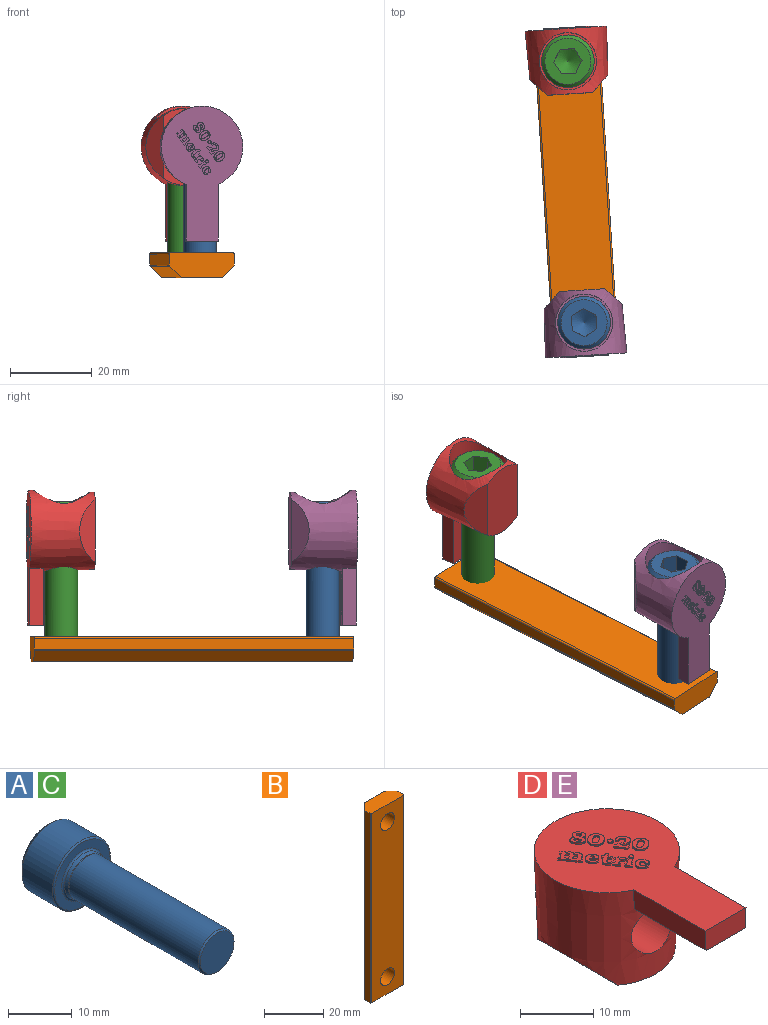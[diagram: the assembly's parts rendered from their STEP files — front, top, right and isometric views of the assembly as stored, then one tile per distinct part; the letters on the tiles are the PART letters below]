
ASSEMBLY  parts=5 mates=5
PART A: 18 faces, bbox 15x38.9x15 mm
  f0: cone r=3.48mm half-angle=60deg, axis (0,1,0), area 43.5mm2, adj f1,f2,f3,f4,f5,f6
  f1: plane 5.51x4.07mm, normal (0.5,0,0.87), area 15mm2, adj f0,f2,f6,f7
  f2: plane 5.51x4.54mm, normal (1,0,0), area 15mm2, adj f0,f1,f3,f7
  f3: plane 5.51x4.07mm, normal (0.5,0,-0.87), area 15mm2, adj f0,f2,f4,f7
  f4: plane 5.51x4.07mm, normal (-0.5,0,-0.87), area 15mm2, adj f0,f3,f5,f7
  f5: plane 5.51x4.54mm, normal (-1,0,0), area 15mm2, adj f0,f4,f6,f7
  f6: plane 5.51x4.07mm, normal (-0.5,0,0.87), area 15mm2, adj f0,f1,f5,f7
  f7: plane 11.27x11.27mm, normal (0,1,0), area 68.5mm2, adj f1,f2,f3,f4,f5,f6,f8
  f8: cone r=6.43mm half-angle=45deg, axis (0,-1,0), area 42.9mm2, adj f7,f9
  f9: cylinder r=6.43mm len=12.87mm, axis (0,-1,0), area 272.9mm2, adj f8,f10
  f10: torus R=6.17mm, axis (0,-1,0), area 16.7mm2, adj f9,f11
  f11: plane 12.33x12.33mm, normal (0,-1,0), area 52.9mm2, adj f10,f12
  f12: torus R=4.6mm, axis (0,-1,0), area 13.9mm2, adj f11,f13
  f13: cone r=4.22mm half-angle=17.9deg, axis (0,1,0), area 16.9mm2, adj f12,f15
  f14: plane 7.5x7.5mm, normal (0,-1,0), area 44.2mm2, adj f16
  f15: torus R=4.4mm, axis (0,-1,0), area 3.1mm2, adj f13,f17
  f16: cone r=4mm half-angle=45deg, axis (0,1,0), area 8.6mm2, adj f14,f17
  f17: cylinder r=4mm len=28.73mm, axis (0,-1,0), area 722.1mm2, adj f15,f16
PART B: 18 faces, bbox 15.9x6.2x78.2 mm
  f0: cylinder r=1.59mm len=3.18mm, axis (0,1,0), area 0mm2, adj f1,f10
  f1: cone r=1.59mm half-angle=59deg, axis (0,1,0), area 9.2mm2, adj f0
  f2: cylinder r=0.38mm len=78.16mm, axis (0,0,1), area 23.4mm2, adj f6,f7,f12,f14
  f3: cylinder r=0.38mm len=78.16mm, axis (0,0,1), area 23.4mm2, adj f8,f9,f12,f14
  f4: cylinder r=0.38mm len=78.16mm, axis (0,0,1), area 23.4mm2, adj f8,f10,f12,f14
  f5: cylinder r=0.38mm len=78.16mm, axis (0,0,1), area 23.4mm2, adj f7,f10,f12,f14
  f6: plane 78.16x2.64mm, normal (1,0,0), area 206.5mm2, adj f2,f11,f12,f14
  f7: plane 78.16x2.76mm, normal (0.71,0.71,0), area 304.6mm2, adj f2,f5,f12,f14
  f8: plane 78.16x2.76mm, normal (-0.71,0.71,0), area 304.6mm2, adj f3,f4,f12,f14
  f9: plane 78.16x2.64mm, normal (-1,0,0), area 206.5mm2, adj f3,f12,f13,f14
  f10: plane 78.16x9.6mm, normal (0,1,0), area 673.1mm2, adj f0,f4,f5,f12,f14,f15,f16
  f11: cylinder r=0.38mm len=78.16mm, axis (0,0,1), area 46.8mm2, adj f6,f12,f14,f17
  f12: plane 15.88x6.16mm, normal (0,0,1), area 88.8mm2, adj f2,f3,f4,f5,f6,f7,f8,f9
  f13: cylinder r=0.38mm len=78.16mm, axis (0,0,1), area 46.8mm2, adj f9,f12,f14,f17
  f14: plane 15.88x6.16mm, normal (0,0,-1), area 88.8mm2, adj f2,f3,f4,f5,f6,f7,f8,f9
  f15: cylinder r=3.32mm len=6.65mm, axis (0,-1,0), area 128.6mm2, adj f10,f17
  f16: cylinder r=3.32mm len=6.65mm, axis (0,1,0), area 128.6mm2, adj f10,f17
  f17: plane 78.16x15.11mm, normal (0,-1,0), area 1111.8mm2, adj f11,f12,f13,f14,f15,f16
PART C: same geometry as A
PART D: 311 faces, bbox 20.2x33.2x16.5 mm
  f0: plane 1.75x1.49mm, normal (0,0,1), area 1.4mm2, adj f8,f9,f10,f11,f12
  f1: plane 0.82x0.69mm, normal (0,0,1), area 0.3mm2, adj f13,f14,f15,f16,f17,f18,f19,f20
  f2: plane 1.07x0.89mm, normal (0,0,1), area 0.5mm2, adj f21,f22,f23,f24,f25,f26
  f3: plane 1.75x1.49mm, normal (0,0,1), area 1.4mm2, adj f27,f28,f29,f30,f31
  f4: plane 0.6x0.53mm, normal (0,0,1), area 0.1mm2, adj f32,f33,f34
  f5: plane 0.91x0.63mm, normal (0,0,-1), area 0.3mm2, adj f35,f36,f37
  f6: plane 1.78x0.94mm, normal (0,0,-1), area 1.1mm2, adj f38,f39,f40,f41,f42
  f7: plane 0.98x0.85mm, normal (0,0,-1), area 0.6mm2, adj f43,f44,f45,f46
  f8: extruded ~1.02x0.29mm, area 0.3mm2, adj f0,f9,f12,f49
  f9: extruded ~0.91x0.54mm, area 0.3mm2, adj f0,f8,f10,f49
  f10: extruded ~1.02x0.3mm, area 0.3mm2, adj f0,f9,f11,f49
  f11: extruded ~0.39x0.25mm, area 0.1mm2, adj f0,f10,f12,f49
  f12: extruded ~0.53x0.51mm, area 0.2mm2, adj f0,f8,f11,f49
  f13: plane 0.25x0.21mm, normal (0.97,0.23,0), area 0.1mm2, adj f1,f14,f20,f50
  f14: extruded ~0.33x0.25mm, area 0.1mm2, adj f1,f13,f15,f50
  f15: cylinder r=0.19mm len=0.25mm, axis (0,0,1), area 0mm2, adj f1,f14,f16,f50
  f16: extruded ~0.4x0.25mm, area 0.1mm2, adj f1,f15,f17,f50
  f17: extruded ~0.46x0.25mm, area 0.1mm2, adj f1,f16,f18,f50
  f18: extruded ~0.25x0.19mm, area 0.1mm2, adj f1,f17,f19,f50
  f19: extruded ~0.25x0.14mm, area 0mm2, adj f1,f18,f20,f50
  f20: plane 0.25x0.1mm, normal (0.13,0.99,0), area 0mm2, adj f1,f13,f19,f50
  f21: plane 0.28x0.25mm, normal (-0.97,-0.23,0), area 0.1mm2, adj f2,f22,f26,f50
  f22: extruded ~0.35x0.25mm, area 0.1mm2, adj f2,f21,f23,f50
  f23: extruded ~0.25x0.14mm, area 0mm2, adj f2,f22,f24,f50
  f24: extruded ~0.51x0.27mm, area 0.2mm2, adj f2,f23,f25,f50
  f25: extruded ~0.59x0.25mm, area 0.2mm2, adj f2,f24,f26,f50
  f26: extruded ~0.52x0.25mm, area 0.1mm2, adj f2,f21,f25,f50
  f27: extruded ~1.02x0.29mm, area 0.3mm2, adj f3,f28,f31,f52
  f28: extruded ~0.91x0.54mm, area 0.3mm2, adj f3,f27,f29,f52
  f29: extruded ~1.02x0.3mm, area 0.3mm2, adj f3,f28,f30,f52
  f30: extruded ~0.39x0.25mm, area 0.1mm2, adj f3,f29,f31,f52
  f31: extruded ~0.53x0.51mm, area 0.2mm2, adj f3,f27,f30,f52
  f32: plane 0.51x0.35mm, normal (0.82,0.57,0), area 0.2mm2, adj f4,f33,f34,f53
  f33: extruded ~0.44x0.25mm, area 0.1mm2, adj f4,f32,f34,f53
  f34: extruded ~0.42x0.25mm, area 0.1mm2, adj f4,f32,f33,f53
  f35: plane 0.63x0.25mm, normal (1,0,0), area 0.2mm2, adj f5,f36,f37,f60
  f36: plane 0.91x0.63mm, normal (-0.57,0.82,0), area 0.3mm2, adj f5,f35,f37,f60
  f37: plane 0.91x0.25mm, normal (0,-1,0), area 0.2mm2, adj f5,f35,f36,f60
  f38: extruded ~0.68x0.25mm, area 0.2mm2, adj f6,f39,f42,f61
  f39: extruded ~0.27x0.25mm, area 0.1mm2, adj f6,f38,f40,f61
  f40: extruded ~0.82x0.4mm, area 0.3mm2, adj f6,f39,f41,f61
  f41: extruded ~0.82x0.4mm, area 0.3mm2, adj f6,f40,f42,f61
  f42: extruded ~0.82x0.4mm, area 0.3mm2, adj f6,f38,f41,f61
  f43: extruded ~0.43x0.4mm, area 0.2mm2, adj f7,f44,f46,f64
  f44: extruded ~0.45x0.39mm, area 0.2mm2, adj f7,f43,f45,f64
  f45: extruded ~0.47x0.38mm, area 0.2mm2, adj f7,f44,f46,f64
  f46: extruded ~0.48x0.41mm, area 0.2mm2, adj f7,f43,f45,f64
  f47: plane 2.21x2.19mm, normal (0,0,1), area 2.1mm2, adj f66,f67,f68,f69,f70,f71,f72,f73
  f48: plane 0.76x0.76mm, normal (0,0,1), area 0.5mm2, adj f78
  f49: plane 2.8x2.67mm, normal (0,0,1), area 3.3mm2, adj f8,f9,f10,f11,f12,f79,f80,f81
  f50: plane 2.86x2.75mm, normal (0,0,1), area 3.5mm2, adj f13,f14,f15,f16,f17,f18,f19,f20
  f51: plane 3.13x2.96mm, normal (0,0,1), area 3.1mm2, adj f94,f95,f96,f97,f98,f99,f100,f101
  f52: plane 2.8x2.67mm, normal (0,0,1), area 3.3mm2, adj f27,f28,f29,f30,f31,f115,f116,f117
  f53: plane 2.1x2.01mm, normal (0,0,1), area 2.3mm2, adj f32,f33,f34,f120,f121,f122,f123,f124
  f54: plane 3.93x3.27mm, normal (0,0,1), area 4.2mm2, adj f129,f130,f131,f132,f133,f134,f135,f136
  f55: plane 2.37x2.3mm, normal (0,0,1), area 1.9mm2, adj f172,f173,f174,f175,f176,f177,f178,f179
  f56: plane 2.41x2.01mm, normal (0,0,1), area 1.7mm2, adj f188,f189,f190,f191,f192,f193,f194,f195
  f57: plane 2.08x1.97mm, normal (0,0,1), area 1.3mm2, adj f208,f209,f210,f211,f212,f213,f214,f215
  f58: plane 0.68x0.67mm, normal (0,0,1), area 0.3mm2, adj f222,f223,f224,f225
  f59: plane 2.1x0.83mm, normal (0,0,-1), area 0.6mm2, adj f227,f228,f229,f230,f231,f232,f233
  f60: plane 2.01x1.39mm, normal (0,0,-1), area 1mm2, adj f35,f36,f37,f234,f235,f236,f237,f238
  f61: plane 2.29x1.56mm, normal (0,0,-1), area 1.1mm2, adj f38,f39,f40,f41,f42,f245,f246,f247
  f62: plane 2.13x1.39mm, normal (0,0,-1), area 1mm2, adj f250,f251,f252,f253,f254,f255,f256,f257
  f63: plane 0.76x0.25mm, normal (0,0,-1), area 0.2mm2, adj f267,f268,f269,f270
  f64: plane 2.29x1.57mm, normal (0,0,-1), area 1.2mm2, adj f43,f44,f45,f46,f271,f272,f273,f274
  f65: plane 2.13x1.39mm, normal (0,0,-1), area 1mm2, adj f283,f284,f285,f286,f287,f288,f289,f290
  f66: extruded ~0.36x0.25mm, area 0.1mm2, adj f47,f67,f77,f302
  f67: extruded ~0.64x0.25mm, area 0.2mm2, adj f47,f66,f68,f302
  f68: extruded ~0.72x0.27mm, area 0.2mm2, adj f47,f67,f69,f302
  f69: extruded ~0.56x0.26mm, area 0.2mm2, adj f47,f68,f70,f302
  f70: plane 0.35x0.25mm, normal (0.99,-0.11,0), area 0.1mm2, adj f47,f69,f71,f302
  f71: extruded ~0.95x0.49mm, area 0.3mm2, adj f47,f70,f72,f302
  f72: extruded ~1.35x0.4mm, area 0.4mm2, adj f47,f71,f73,f302
  f73: extruded ~1.38x0.47mm, area 0.4mm2, adj f47,f72,f74,f302
  f74: extruded ~1x0.25mm, area 0.3mm2, adj f47,f73,f75,f302
  f75: extruded ~0.42x0.25mm, area 0.1mm2, adj f47,f74,f76,f302
  f76: extruded ~0.25x0.23mm, area 0.1mm2, adj f47,f75,f77,f302
  f77: extruded ~0.25x0.12mm, area 0mm2, adj f47,f66,f76,f302
  f78: cylinder r=0.38mm len=0.76mm, axis (0,0,1), area 0.6mm2, adj f48,f302
  f79: extruded ~1.72x0.48mm, area 0.5mm2, adj f49,f80,f83,f302
  f80: extruded ~1.64x0.63mm, area 0.5mm2, adj f49,f79,f81,f302
  f81: extruded ~0.68x0.32mm, area 0.2mm2, adj f49,f80,f82,f302
  f82: extruded ~1.06x0.48mm, area 0.3mm2, adj f49,f81,f83,f302
  f83: extruded ~1.66x0.66mm, area 0.5mm2, adj f49,f79,f82,f302
  f84: extruded ~0.74x0.27mm, area 0.2mm2, adj f50,f85,f93,f302
  f85: extruded ~1.14x0.5mm, area 0.3mm2, adj f50,f84,f86,f302
  f86: extruded ~1.09x0.25mm, area 0.3mm2, adj f50,f85,f87,f302
  f87: extruded ~0.7x0.25mm, area 0.2mm2, adj f50,f86,f88,f302
  f88: extruded ~0.53x0.25mm, area 0.1mm2, adj f50,f87,f89,f302
  f89: extruded ~0.31x0.25mm, area 0.1mm2, adj f50,f88,f90,f302
  f90: extruded ~0.6x0.25mm, area 0.2mm2, adj f50,f89,f91,f302
  f91: extruded ~0.65x0.51mm, area 0.2mm2, adj f50,f90,f92,f302
  f92: extruded ~1.25x0.27mm, area 0.4mm2, adj f50,f91,f93,f302
  f93: extruded ~0.8x0.25mm, area 0.2mm2, adj f50,f84,f92,f302
  f94: plane 0.25x0.07mm, normal (-0.75,0.66,0), area 0mm2, adj f51,f95,f114,f302
  f95: plane 1.38x0.96mm, normal (-0.82,-0.57,0), area 0.4mm2, adj f51,f94,f96,f302
  f96: plane 0.29x0.25mm, normal (-0.57,0.82,0), area 0.1mm2, adj f51,f95,f97,f302
  f97: extruded ~1.12x0.36mm, area 0.3mm2, adj f51,f96,f98,f302
  f98: extruded ~0.56x0.25mm, area 0.1mm2, adj f51,f97,f99,f302
  f99: cylinder r=0.53mm len=0.26mm, axis (0,0,-1), area 0.1mm2, adj f51,f98,f100,f302
  f100: extruded ~0.63x0.25mm, area 0.2mm2, adj f51,f99,f101,f302
  f101: extruded ~0.7x0.26mm, area 0.2mm2, adj f51,f100,f102,f302
  f102: cylinder r=1.31mm len=0.25mm, axis (0,0,-1), area 0mm2, adj f51,f101,f103,f302
  f103: plane 0.28x0.25mm, normal (-0.77,-0.64,0), area 0.1mm2, adj f51,f102,f104,f302
  f104: cylinder r=0.84mm len=0.25mm, axis (0,0,1), area 0mm2, adj f51,f103,f105,f302
  f105: extruded ~1.36x0.53mm, area 0.4mm2, adj f51,f104,f106,f302
  f106: extruded ~1.25x0.28mm, area 0.4mm2, adj f51,f105,f107,f302
  f107: extruded ~0.35x0.25mm, area 0.1mm2, adj f51,f106,f108,f302
  f108: extruded ~1.42x0.42mm, area 0.4mm2, adj f51,f107,f109,f302
  f109: plane 0.5x0.35mm, normal (0.82,0.57,0), area 0.2mm2, adj f51,f108,f110,f302
  f110: extruded ~0.37x0.25mm, area 0.1mm2, adj f51,f109,f111,f302
  f111: plane 0.25x0.08mm, normal (-0.42,0.91,0), area 0mm2, adj f51,f110,f112,f302
  f112: plane 0.29x0.25mm, normal (0.82,0.57,0), area 0.1mm2, adj f51,f111,f113,f302
  f113: plane 0.86x0.4mm, normal (0.42,-0.91,0), area 0.2mm2, adj f51,f112,f114,f302
  f114: plane 0.25x0.2mm, normal (-0.82,-0.57,0), area 0.1mm2, adj f51,f94,f113,f302
  f115: extruded ~1.66x0.66mm, area 0.5mm2, adj f52,f116,f119,f302
  f116: extruded ~1.72x0.48mm, area 0.5mm2, adj f52,f115,f117,f302
  f117: extruded ~1.64x0.63mm, area 0.5mm2, adj f52,f116,f118,f302
  f118: extruded ~0.68x0.32mm, area 0.2mm2, adj f52,f117,f119,f302
  f119: extruded ~1.06x0.48mm, area 0.3mm2, adj f52,f115,f118,f302
  f120: plane 1x0.7mm, normal (-0.82,-0.57,0), area 0.3mm2, adj f53,f121,f128,f302
  f121: extruded ~0.67x0.25mm, area 0.2mm2, adj f53,f120,f122,f302
  f122: extruded ~0.56x0.28mm, area 0.2mm2, adj f53,f121,f123,f302
  f123: plane 0.35x0.25mm, normal (0.98,-0.18,0), area 0.1mm2, adj f53,f122,f124,f302
  f124: extruded ~0.91x0.49mm, area 0.3mm2, adj f53,f123,f125,f302
  f125: extruded ~1.36x0.41mm, area 0.4mm2, adj f53,f124,f126,f302
  f126: extruded ~1.34x0.45mm, area 0.4mm2, adj f53,f125,f127,f302
  f127: extruded ~1.13x0.28mm, area 0.3mm2, adj f53,f126,f128,f302
  f128: extruded ~0.25x0.19mm, area 0.1mm2, adj f53,f120,f127,f302
  f129: plane 0.29x0.25mm, normal (-0.57,0.82,0), area 0.1mm2, adj f54,f130,f171,f302
  f130: extruded ~0.27x0.25mm, area 0.1mm2, adj f54,f129,f131,f302
  f131: plane 0.51x0.36mm, normal (-0.57,0.82,0), area 0.2mm2, adj f54,f130,f132,f302
  f132: extruded ~0.25x0.14mm, area 0mm2, adj f54,f131,f133,f302
  f133: extruded ~0.25x0.16mm, area 0mm2, adj f54,f132,f134,f302
  f134: cylinder r=0.48mm len=0.25mm, axis (0,0,-1), area 0.1mm2, adj f54,f133,f135,f302
  f135: extruded ~0.25x0.16mm, area 0mm2, adj f54,f134,f136,f302
  f136: plane 0.25x0.05mm, normal (-0.37,-0.93,0), area 0mm2, adj f54,f135,f137,f302
  f137: plane 0.58x0.41mm, normal (0.57,-0.82,0), area 0.2mm2, adj f54,f136,f138,f302
  f138: extruded ~0.25x0.24mm, area 0.1mm2, adj f54,f137,f139,f302
  f139: plane 0.25x0.04mm, normal (0.82,0.57,0), area 0mm2, adj f54,f138,f140,f302
  f140: plane 0.29x0.25mm, normal (0.57,-0.82,0), area 0.1mm2, adj f54,f139,f141,f302
  f141: plane 0.87x0.61mm, normal (-0.82,-0.57,0), area 0.3mm2, adj f54,f140,f142,f302
  f142: plane 0.29x0.25mm, normal (-0.57,0.82,0), area 0.1mm2, adj f54,f141,f143,f302
  f143: plane 0.25x0.06mm, normal (0.82,0.57,0), area 0mm2, adj f54,f142,f144,f302
  f144: extruded ~0.27x0.25mm, area 0.1mm2, adj f54,f143,f145,f302
  f145: plane 0.67x0.47mm, normal (-0.57,0.82,0), area 0.2mm2, adj f54,f144,f146,f302
  f146: plane 0.25x0.22mm, normal (-0.82,-0.57,0), area 0.1mm2, adj f54,f145,f147,f302
  f147: plane 0.29x0.25mm, normal (-0.57,0.82,0), area 0.1mm2, adj f54,f146,f148,f302
  f148: extruded ~0.48x0.42mm, area 0.2mm2, adj f54,f147,f149,f302
  f149: plane 0.25x0.14mm, normal (0.82,0.57,0), area 0mm2, adj f54,f148,f150,f302
  f150: plane 0.25x0.2mm, normal (0.57,-0.82,0), area 0.1mm2, adj f54,f149,f151,f302
  f151: extruded ~0.57x0.4mm, area 0.2mm2, adj f54,f150,f152,f302
  f152: extruded ~0.55x0.25mm, area 0.1mm2, adj f54,f151,f153,f302
  f153: extruded ~0.59x0.4mm, area 0.2mm2, adj f54,f152,f154,f302
  f154: extruded ~0.67x0.25mm, area 0.2mm2, adj f54,f153,f155,f302
  f155: extruded ~0.25x0.15mm, area 0mm2, adj f54,f154,f156,f302
  f156: plane 0.62x0.43mm, normal (0.57,-0.82,0), area 0.2mm2, adj f54,f155,f157,f302
  f157: extruded ~0.25x0.14mm, area 0mm2, adj f54,f156,f158,f302
  f158: extruded ~0.25x0.11mm, area 0mm2, adj f54,f157,f159,f302
  f159: plane 0.25x0.07mm, normal (0.82,0.57,0), area 0mm2, adj f54,f158,f160,f302
  f160: plane 0.29x0.25mm, normal (0.57,-0.82,0), area 0.1mm2, adj f54,f159,f161,f302
  f161: plane 0.87x0.61mm, normal (-0.82,-0.57,0), area 0.3mm2, adj f54,f160,f162,f302
  f162: plane 0.29x0.25mm, normal (-0.57,0.82,0), area 0.1mm2, adj f54,f161,f163,f302
  f163: extruded ~0.26x0.25mm, area 0.1mm2, adj f54,f162,f164,f302
  f164: plane 0.54x0.38mm, normal (-0.57,0.82,0), area 0.2mm2, adj f54,f163,f165,f302
  f165: extruded ~0.29x0.25mm, area 0.1mm2, adj f54,f164,f166,f302
  f166: extruded ~0.37x0.25mm, area 0.1mm2, adj f54,f165,f167,f302
  f167: plane 0.58x0.41mm, normal (0.57,-0.82,0), area 0.2mm2, adj f54,f166,f168,f302
  f168: extruded ~0.25x0.15mm, area 0.1mm2, adj f54,f167,f169,f302
  f169: extruded ~0.25x0.12mm, area 0mm2, adj f54,f168,f170,f302
  f170: plane 0.29x0.25mm, normal (0.57,-0.82,0), area 0.1mm2, adj f54,f169,f171,f302
  f171: plane 0.81x0.57mm, normal (-0.82,-0.57,0), area 0.3mm2, adj f54,f129,f170,f302
  f172: extruded ~0.9x0.26mm, area 0.3mm2, adj f55,f173,f187,f302
  f173: plane 0.71x0.5mm, normal (-0.57,0.82,0), area 0.2mm2, adj f55,f172,f174,f302
  f174: plane 0.25x0.22mm, normal (-0.82,-0.57,0), area 0.1mm2, adj f55,f173,f175,f302
  f175: plane 0.29x0.25mm, normal (-0.57,0.82,0), area 0.1mm2, adj f55,f174,f176,f302
  f176: extruded ~0.83x0.25mm, area 0.2mm2, adj f55,f175,f177,f302
  f177: plane 0.29x0.25mm, normal (0.82,0.57,0), area 0.1mm2, adj f55,f176,f178,f302
  f178: plane 0.51x0.36mm, normal (0.57,-0.82,0), area 0.2mm2, adj f55,f177,f179,f302
  f179: plane 0.48x0.34mm, normal (0.82,0.57,0), area 0.1mm2, adj f55,f178,f180,f302
  f180: plane 0.32x0.25mm, normal (0.57,-0.82,0), area 0.1mm2, adj f55,f179,f181,f302
  f181: plane 0.48x0.34mm, normal (-0.82,-0.57,0), area 0.1mm2, adj f55,f180,f182,f302
  f182: plane 0.52x0.36mm, normal (0.57,-0.82,0), area 0.2mm2, adj f55,f181,f183,f302
  f183: extruded ~0.3x0.25mm, area 0.1mm2, adj f55,f182,f184,f302
  f184: extruded ~0.25x0.18mm, area 0mm2, adj f55,f183,f185,f302
  f185: extruded ~0.31x0.25mm, area 0.1mm2, adj f55,f184,f186,f302
  f186: plane 0.32x0.25mm, normal (0.57,-0.82,0), area 0.1mm2, adj f55,f185,f187,f302
  f187: extruded ~0.43x0.38mm, area 0.1mm2, adj f55,f172,f186,f302
  f188: plane 0.92x0.64mm, normal (-0.82,-0.57,0), area 0.3mm2, adj f56,f189,f207,f302
  f189: plane 0.29x0.25mm, normal (-0.57,0.82,0), area 0.1mm2, adj f56,f188,f190,f302
  f190: plane 0.25x0.08mm, normal (0.82,0.57,0), area 0mm2, adj f56,f189,f191,f302
  f191: extruded ~0.25x0.24mm, area 0.1mm2, adj f56,f190,f192,f302
  f192: plane 0.69x0.48mm, normal (-0.57,0.82,0), area 0.2mm2, adj f56,f191,f193,f302
  f193: plane 0.25x0.22mm, normal (-0.82,-0.57,0), area 0.1mm2, adj f56,f192,f194,f302
  f194: plane 0.28x0.25mm, normal (-0.57,0.82,0), area 0.1mm2, adj f56,f193,f195,f302
  f195: extruded ~0.48x0.42mm, area 0.2mm2, adj f56,f194,f196,f302
  f196: plane 0.25x0.14mm, normal (0.82,0.57,0), area 0mm2, adj f56,f195,f197,f302
  f197: plane 0.25x0.22mm, normal (0.57,-0.82,0), area 0.1mm2, adj f56,f196,f198,f302
  f198: extruded ~0.48x0.25mm, area 0.1mm2, adj f56,f197,f199,f302
  f199: extruded ~0.44x0.25mm, area 0.1mm2, adj f56,f198,f200,f302
  f200: extruded ~0.41x0.25mm, area 0.1mm2, adj f56,f199,f201,f302
  f201: extruded ~0.25x0.18mm, area 0mm2, adj f56,f200,f202,f302
  f202: extruded ~0.25x0.07mm, area 0mm2, adj f56,f201,f203,f302
  f203: extruded ~0.25x0.14mm, area 0mm2, adj f56,f202,f204,f302
  f204: plane 0.58x0.41mm, normal (0.57,-0.82,0), area 0.2mm2, adj f56,f203,f205,f302
  f205: extruded ~0.26x0.25mm, area 0.1mm2, adj f56,f204,f206,f302
  f206: plane 0.25x0.07mm, normal (0.82,0.57,0), area 0mm2, adj f56,f205,f207,f302
  f207: plane 0.29x0.25mm, normal (0.57,-0.82,0), area 0.1mm2, adj f56,f188,f206,f302
  f208: plane 0.25x0.22mm, normal (-0.82,-0.57,0), area 0.1mm2, adj f57,f209,f221,f302
  f209: plane 0.28x0.25mm, normal (-0.57,0.82,0), area 0.1mm2, adj f57,f208,f210,f302
  f210: extruded ~0.37x0.36mm, area 0.1mm2, adj f57,f209,f211,f302
  f211: extruded ~0.25x0.16mm, area 0mm2, adj f57,f210,f212,f302
  f212: plane 0.25x0.14mm, normal (0.82,0.57,0), area 0mm2, adj f57,f211,f213,f302
  f213: plane 1.1x0.77mm, normal (0.57,-0.82,0), area 0.3mm2, adj f57,f212,f214,f302
  f214: extruded ~0.25x0.24mm, area 0.1mm2, adj f57,f213,f215,f302
  f215: plane 0.25x0.08mm, normal (0.82,0.57,0), area 0mm2, adj f57,f214,f216,f302
  f216: plane 0.29x0.25mm, normal (0.57,-0.82,0), area 0.1mm2, adj f57,f215,f217,f302
  f217: plane 0.92x0.64mm, normal (-0.82,-0.57,0), area 0.3mm2, adj f57,f216,f218,f302
  f218: plane 0.29x0.25mm, normal (-0.57,0.82,0), area 0.1mm2, adj f57,f217,f219,f302
  f219: plane 0.25x0.08mm, normal (0.82,0.57,0), area 0mm2, adj f57,f218,f220,f302
  f220: extruded ~0.25x0.21mm, area 0.1mm2, adj f57,f219,f221,f302
  f221: plane 0.71x0.5mm, normal (-0.57,0.82,0), area 0.2mm2, adj f57,f208,f220,f302
  f222: extruded ~0.47x0.25mm, area 0.1mm2, adj f58,f223,f225,f302
  f223: extruded ~0.46x0.25mm, area 0.1mm2, adj f58,f222,f224,f302
  f224: extruded ~0.47x0.25mm, area 0.1mm2, adj f58,f223,f225,f302
  f225: extruded ~0.46x0.25mm, area 0.1mm2, adj f58,f222,f224,f302
  f226: plane 7.85x3.3mm, normal (0,-1,0), area 25.5mm2, adj f301,f302,f303,f304
  f227: plane 0.25x0.16mm, normal (1,0,0), area 0mm2, adj f59,f228,f233,f304
  f228: plane 2.01x0.25mm, normal (0,1,0), area 0.5mm2, adj f59,f227,f229,f304
  f229: plane 0.25x0.25mm, normal (-1,0,0), area 0.1mm2, adj f59,f228,f230,f304
  f230: plane 1.57x0.25mm, normal (0,-1,0), area 0.4mm2, adj f59,f229,f231,f304
  f231: extruded ~0.49x0.3mm, area 0.1mm2, adj f59,f230,f232,f304
  f232: plane 0.25x0.24mm, normal (0,-1,0), area 0.1mm2, adj f59,f231,f233,f304
  f233: extruded ~0.58x0.5mm, area 0.2mm2, adj f59,f227,f232,f304
  f234: plane 0.25x0.23mm, normal (0,1,0), area 0.1mm2, adj f60,f235,f244,f304
  f235: plane 0.27x0.25mm, normal (-1,0,0), area 0.1mm2, adj f60,f234,f236,f304
  f236: plane 0.48x0.25mm, normal (0,1,0), area 0.1mm2, adj f60,f235,f237,f304
  f237: plane 0.25x0.25mm, normal (-1,0,0), area 0.1mm2, adj f60,f236,f238,f304
  f238: plane 0.48x0.25mm, normal (0,-1,0), area 0.1mm2, adj f60,f237,f239,f304
  f239: plane 0.87x0.25mm, normal (-1,0,0), area 0.2mm2, adj f60,f238,f240,f304
  f240: plane 0.25x0.23mm, normal (0,-1,0), area 0.1mm2, adj f60,f239,f241,f304
  f241: plane 1.3x0.91mm, normal (0.58,-0.82,0), area 0.4mm2, adj f60,f240,f242,f304
  f242: plane 0.25x0.2mm, normal (1,0,0), area 0.1mm2, adj f60,f241,f243,f304
  f243: plane 1.3x0.25mm, normal (0,1,0), area 0.3mm2, adj f60,f242,f244,f304
  f244: plane 0.27x0.25mm, normal (1,0,0), area 0.1mm2, adj f60,f234,f243,f304
  f245: extruded ~0.46x0.25mm, area 0.1mm2, adj f61,f246,f249,f304
  f246: extruded ~0.82x0.25mm, area 0.2mm2, adj f61,f245,f247,f304
  f247: extruded ~1.02x0.65mm, area 0.3mm2, adj f61,f246,f248,f304
  f248: extruded ~1.02x0.65mm, area 0.3mm2, adj f61,f247,f249,f304
  f249: extruded ~1.02x0.65mm, area 0.3mm2, adj f61,f245,f248,f304
  f250: plane 0.25x0.25mm, normal (-0.98,-0.18,0), area 0.1mm2, adj f62,f251,f266,f304
  f251: extruded ~0.6x0.52mm, area 0.2mm2, adj f62,f250,f252,f304
  f252: extruded ~0.59x0.52mm, area 0.2mm2, adj f62,f251,f253,f304
  f253: extruded ~0.41x0.28mm, area 0.1mm2, adj f62,f252,f254,f304
  f254: extruded ~0.49x0.37mm, area 0.2mm2, adj f62,f253,f255,f304
  f255: extruded ~0.68x0.63mm, area 0.3mm2, adj f62,f254,f256,f304
  f256: extruded ~0.64x0.57mm, area 0.2mm2, adj f62,f255,f257,f304
  f257: plane 0.25x0.25mm, normal (0.99,-0.13,0), area 0.1mm2, adj f62,f256,f258,f304
  f258: extruded ~0.39x0.39mm, area 0.2mm2, adj f62,f257,f259,f304
  f259: extruded ~0.42x0.41mm, area 0.2mm2, adj f62,f258,f260,f304
  f260: extruded ~0.39x0.39mm, area 0.2mm2, adj f62,f259,f261,f304
  f261: extruded ~0.25x0.17mm, area 0mm2, adj f62,f260,f262,f304
  f262: plane 0.25x0.22mm, normal (0.12,-0.99,0), area 0.1mm2, adj f62,f261,f263,f304
  f263: cylinder r=0.27mm len=0.25mm, axis (0,0,1), area 0mm2, adj f62,f262,f264,f304
  f264: extruded ~0.41x0.34mm, area 0.2mm2, adj f62,f263,f265,f304
  f265: extruded ~0.33x0.31mm, area 0.1mm2, adj f62,f264,f266,f304
  f266: extruded ~0.36x0.36mm, area 0.1mm2, adj f62,f250,f265,f304
  f267: plane 0.76x0.25mm, normal (-1,0,0), area 0.2mm2, adj f63,f268,f270,f304
  f268: plane 0.25x0.25mm, normal (0,-1,0), area 0.1mm2, adj f63,f267,f269,f304
  f269: plane 0.76x0.25mm, normal (1,0,0), area 0.2mm2, adj f63,f268,f270,f304
  f270: plane 0.25x0.25mm, normal (0,1,0), area 0.1mm2, adj f63,f267,f269,f304
  f271: extruded ~0.97x0.7mm, area 0.3mm2, adj f64,f272,f282,f304
  f272: extruded ~0.85x0.25mm, area 0.2mm2, adj f64,f271,f273,f304
  f273: extruded ~0.5x0.25mm, area 0.1mm2, adj f64,f272,f274,f304
  f274: extruded ~0.57x0.5mm, area 0.2mm2, adj f64,f273,f275,f304
  f275: plane 0.25x0.24mm, normal (-1,0.08,0), area 0.1mm2, adj f64,f274,f276,f304
  f276: extruded ~0.25x0.21mm, area 0.1mm2, adj f64,f275,f277,f304
  f277: cylinder r=0.33mm len=0.25mm, axis (0,0,1), area 0.1mm2, adj f64,f276,f278,f304
  f278: extruded ~0.25x0.21mm, area 0.1mm2, adj f64,f277,f279,f304
  f279: extruded ~0.71x0.25mm, area 0.2mm2, adj f64,f278,f280,f304
  f280: extruded ~0.49x0.27mm, area 0.1mm2, adj f64,f279,f281,f304
  f281: extruded ~0.65x0.59mm, area 0.2mm2, adj f64,f280,f282,f304
  f282: extruded ~0.69x0.63mm, area 0.3mm2, adj f64,f271,f281,f304
  f283: extruded ~0.36x0.36mm, area 0.1mm2, adj f65,f284,f299,f304
  f284: plane 0.25x0.25mm, normal (-0.98,-0.18,0), area 0.1mm2, adj f65,f283,f285,f304
  f285: extruded ~0.6x0.52mm, area 0.2mm2, adj f65,f284,f286,f304
  f286: extruded ~0.59x0.52mm, area 0.2mm2, adj f65,f285,f287,f304
  f287: extruded ~0.41x0.28mm, area 0.1mm2, adj f65,f286,f288,f304
  f288: extruded ~0.49x0.37mm, area 0.2mm2, adj f65,f287,f289,f304
  f289: extruded ~0.68x0.63mm, area 0.3mm2, adj f65,f288,f290,f304
  f290: extruded ~0.64x0.57mm, area 0.2mm2, adj f65,f289,f291,f304
  f291: plane 0.25x0.25mm, normal (0.99,-0.13,0), area 0.1mm2, adj f65,f290,f292,f304
  f292: extruded ~0.39x0.39mm, area 0.2mm2, adj f65,f291,f293,f304
  f293: extruded ~0.42x0.41mm, area 0.2mm2, adj f65,f292,f294,f304
  f294: extruded ~0.39x0.39mm, area 0.2mm2, adj f65,f293,f295,f304
  f295: extruded ~0.25x0.17mm, area 0mm2, adj f65,f294,f296,f304
  f296: plane 0.25x0.22mm, normal (0.12,-0.99,0), area 0.1mm2, adj f65,f295,f297,f304
  f297: cylinder r=0.27mm len=0.25mm, axis (0,0,1), area 0mm2, adj f65,f296,f298,f304
  f298: extruded ~0.41x0.34mm, area 0.2mm2, adj f65,f297,f299,f304
  f299: extruded ~0.33x0.31mm, area 0.1mm2, adj f65,f283,f298,f304
  f300: plane 13.97x13.97mm, normal (0,1,0), area 101.4mm2, adj f305,f306
  f301: plane 13.94x3.3mm, normal (-1,0,-0.03), area 45.9mm2, adj f226,f302,f304,f310
  f302: plane 33.2x20.14mm, normal (0,0,1), area 385.3mm2, adj f66,f67,f68,f69,f70,f71,f72,f73
  f303: plane 13.94x3.3mm, normal (1,0,-0.03), area 45.9mm2, adj f226,f302,f304,f310
  f304: plane 14.18x7.86mm, normal (0,0,-1), area 94.1mm2, adj f226,f227,f228,f229,f230,f231,f232,f233
  f305: cylinder r=6.99mm len=13.97mm, axis (0,1,0), area 393.1mm2, adj f300,f310
  f306: cylinder r=4.06mm len=9.12mm, axis (0,1,0), area 219.7mm2, adj f300,f310
  f307: plane 15.29x4.06mm, normal (0.71,0,-0.71), area 61.8mm2, adj f309,f310
  f308: plane 15.29x4.06mm, normal (-0.71,0,-0.71), area 61.8mm2, adj f309,f310
  f309: plane 18.82x10.98mm, normal (0,0,-1), area 194.3mm2, adj f307,f308,f310
  f310: cone r=9.97mm half-angle=2deg, axis (0,0,1), area 632.3mm2, adj f301,f302,f303,f304,f305,f306,f307,f308
PART E: same geometry as D
PLACE A rot(axis=(0.02,-0.71,-0.71),177.5deg) t=(2.44,-32.8,29.5)mm
PLACE B rot(axis=(-1,-0.03,0.03),90.1deg) t=(0.46,-0.86,4.34)mm
PLACE C rot(axis=(0.6,-0.57,-0.57),118deg) t=(-1.52,31.08,29.5)mm
PLACE D rot(axis=(0.02,-0.71,-0.71),177.5deg) t=(-1.91,37.42,30.22)mm
PLACE E rot(axis=(1,0.03,0.03),90.1deg) t=(2.83,-39.14,30.22)mm
MATE slider A.f16 <-> B.f15  axis (0,0,-1) through (2.44,-32.8,-0.5)mm
MATE planar C.f16 <-> A.f16  axis (0,0,-1) through (-1.52,31.08,-0.5)mm
MATE fastened C.f0 <-> D.f305  axis (0,0,-1) through (-1.52,31.08,29.5)mm
MATE slider C.f16 <-> B.f16  axis (0,0,-1) through (-1.52,31.08,-0.5)mm
MATE fastened A.f0 <-> E.f305  axis (0,0,-1) through (2.44,-32.8,29.5)mm
